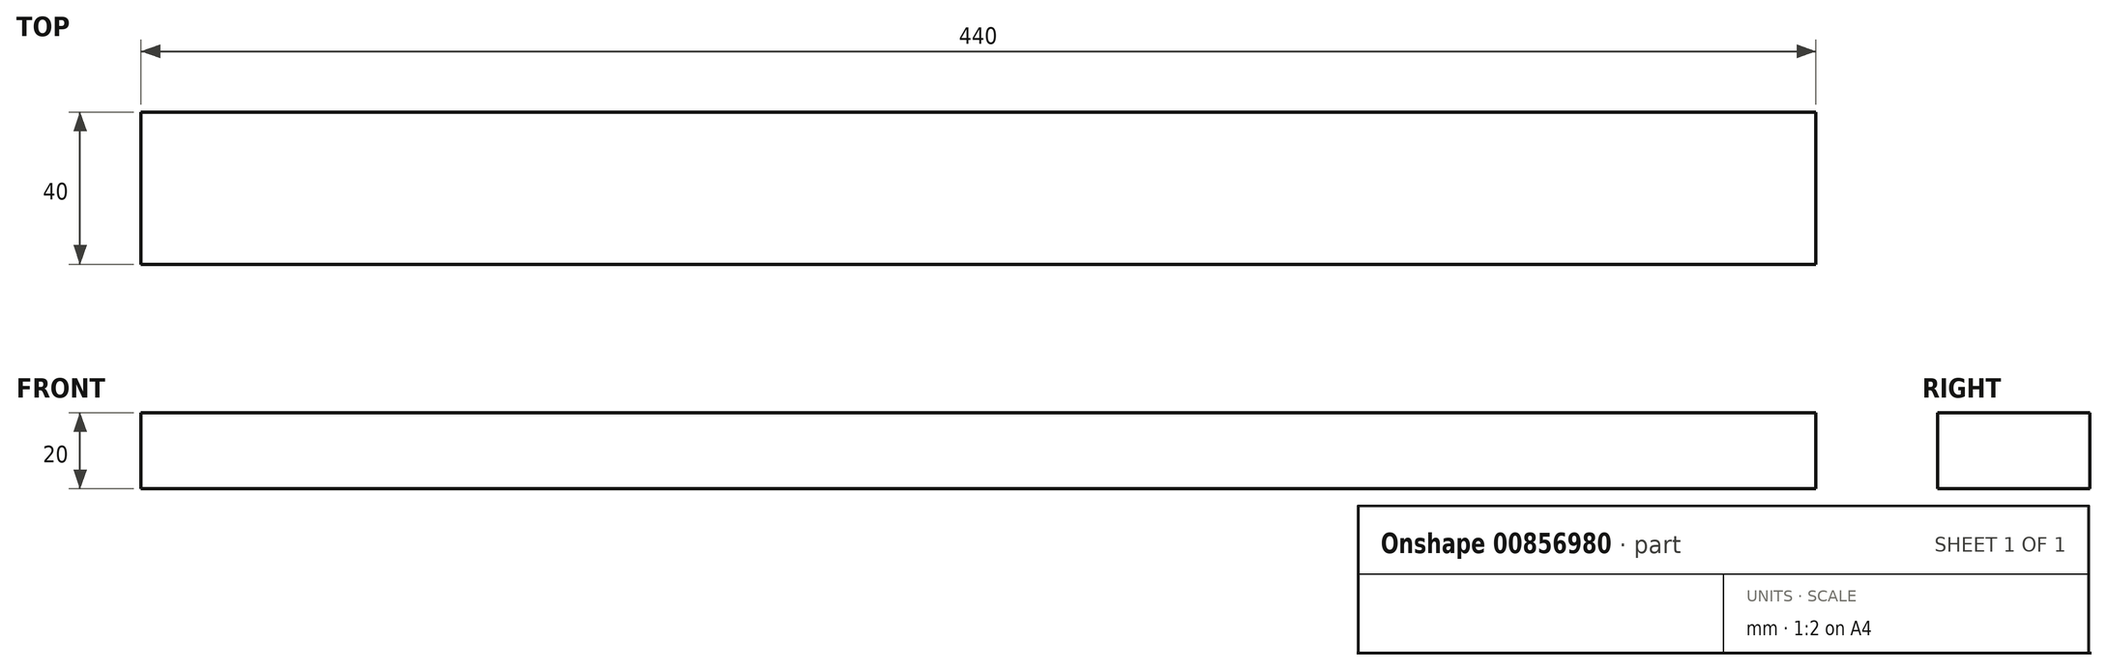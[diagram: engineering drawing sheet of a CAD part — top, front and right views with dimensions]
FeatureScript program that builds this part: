
annotation { "Feature Type Name" : "Feature", "Feature Type Description" : "" }
export const myFeature = defineFeature(function(context is Context, id is Id, definition is map)
    precondition{}
    {
        {
            var Q0;
            Q0=qCreatedBy(makeId("Right.planeOp"),FACE);
            var sketch = newSketch(context, id + "F0", { "sketchPlane" : qUnion([Q0])});
            skLineSegment(sketch, "E0.bottom", {"start": v(0, 0) * mm, "end": v(40, 0) * mm});
            skLineSegment(sketch, "E0.top", {"start": v(0, -20) * mm, "end": v(40, -20) * mm});
            skLineSegment(sketch, "E0.left", {"start": v(0, 0) * mm, "end": v(0, -20) * mm});
            skLineSegment(sketch, "E0.right", {"start": v(40, 0) * mm, "end": v(40, -20) * mm});
            skSolve(sketch);
        }
        {
            var Q0;
            Q0=makeQuery(id+"F0.imprint","IMPRINT",FACE,{"disambiguationData":[TD([[makeQuery(id+"F0.imprint","IMPRINT",EDGE,{"derivedFrom":sQuery(id+"F0.wireOp",EDGE,"E0.bottom")}),-1.0]])]});
            extrude(context, id + "F1", {"entities" : qUnion([Q0]), "depth" : 440 * mm, "offsetDistance" : 25 * mm});
        }
        {
            var Q0;
            Q0=makeQuery(id+"F1.opExtrude","SWEPT_FACE",FACE,{"disambiguationData":[OSD([sQuery(id+"F0.wireOp",EDGE,"E0.left")])]});
            var sketch = newSketch(context, id + "F2", { "sketchPlane" : qUnion([Q0])});
            skLineSegment(sketch, "E1", {"start": v(0, -10) * mm, "end": v(20, -10) * mm, "construction": true});
            skLineSegment(sketch, "E2", {"start": v(440, -10) * mm, "end": v(420, -10) * mm, "construction": true});
            skSolve(sketch);
        }
        {
            var Q0;
            Q0=makeQuery(id+"F1.opExtrude","SWEPT_FACE",FACE,{"disambiguationData":[OSD([sQuery(id+"F0.wireOp",EDGE,"E0.right")])]});
            var sketch = newSketch(context, id + "F3", { "sketchPlane" : qUnion([Q0])});
            skLineSegment(sketch, "E3", {"start": v(-440, -10) * mm, "end": v(-420, -10) * mm, "construction": true});
            skLineSegment(sketch, "E4", {"start": v(0, -10) * mm, "end": v(-20, -10) * mm, "construction": true});
            skSolve(sketch);
        }
    });
